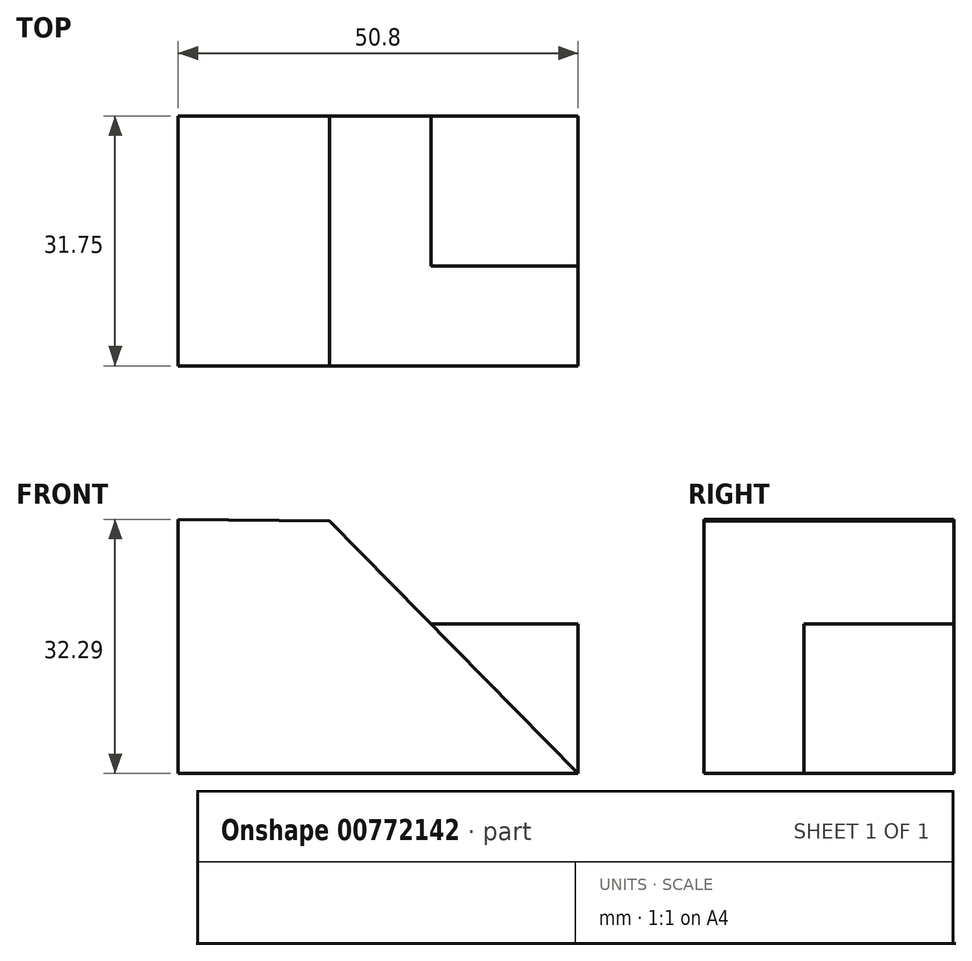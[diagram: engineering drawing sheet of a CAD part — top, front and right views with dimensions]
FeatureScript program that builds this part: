
annotation { "Feature Type Name" : "Feature", "Feature Type Description" : "" }
export const myFeature = defineFeature(function(context is Context, id is Id, definition is map)
    precondition{}
    {
        {
            var Q0;
            Q0=qCreatedBy(makeId("Front.planeOp"),FACE);
            var sketch = newSketch(context, id + "F0", { "sketchPlane" : qUnion([Q0])});
            skLineSegment(sketch, "E0", {"start": v(0, 32.3) * mm, "end": v(0, 0) * mm});
            skLineSegment(sketch, "E1", {"start": v(0, 0) * mm, "end": v(50.8, 0) * mm});
            skLineSegment(sketch, "E2", {"start": v(50.8, 0) * mm, "end": v(50.8, 31.75) * mm});
            skLineSegment(sketch, "E3", {"start": v(50.8, 31.75) * mm, "end": v(0, 32.3) * mm});
            skSolve(sketch);
        }
        {
            var Q0;
            Q0 = qSketchRegion(id + "F0", true);
            extrude(context, id + "F1", {"entities" : qUnion([Q0]), "depth" : 31.75 * mm, "offsetDistance" : 25.4 * mm});
        }
        {
            var Q0;
            Q0=makeQuery(id+"F1.opExtrude","CAP_FACE",FACE,{"disambiguationData":[OSD([sQuery(id+"F0.wireOp",EDGE,"E0"),sQuery(id+"F0.wireOp",EDGE,"E1"),sQuery(id+"F0.wireOp",EDGE,"E2"),sQuery(id+"F0.wireOp",EDGE,"E3")])],"isStart":false});
            var sketch = newSketch(context, id + "F2", { "sketchPlane" : qUnion([Q0])});
            skLineSegment(sketch, "E4", {"start": v(0, 32.3) * mm, "end": v(19.2, 32.09) * mm});
            skLineSegment(sketch, "E5", {"start": v(19.2, 32.09) * mm, "end": v(50.8, 0) * mm});
            skSolve(sketch);
        }
        {
            var Q0;
            {var subQ0=sQuery(id+"F2.wireOp",EDGE,"E5");Q0=makeQuery(id+"F2.imprint","IMPRINT",FACE,{"disambiguationData":[TD([[makeQuery(id+"F2.imprint","IMPRINT",EDGE,{"derivedFrom":subQ0}),1.0]])]});}
            extrude(context, id + "F3", {"entities" : qUnion([Q0]), "operationType" : NewBodyOperationType.REMOVE, "oppositeDirection" : true, "depth" : 12.7 * mm, "offsetDistance" : 25.4 * mm});
        }
        {
            var Q0;
            Q0=makeQuery(id+"F3.boolean.opBoolean","COPY",FACE,{"derivedFrom":makeQuery(id+"F3.opExtrude","CAP_FACE",FACE,{"disambiguationData":[OSD([sQuery(id+"F0.wireOp",EDGE,"E2"),sQuery(id+"F0.wireOp",EDGE,"E3"),sQuery(id+"F2.wireOp",EDGE,"E5")])],"isStart":false})});
            var sketch = newSketch(context, id + "F4", { "sketchPlane" : qUnion([Q0])});
            skLineSegment(sketch, "E6", {"start": v(50.8, 0) * mm, "end": v(50.8, 19) * mm});
            skLineSegment(sketch, "E7", {"start": v(50.8, 19) * mm, "end": v(32.1, 19) * mm});
            skSolve(sketch);
        }
        {
            var Q0;
            {var subQ0=sQuery(id+"F4.wireOp",EDGE,"E7");Q0=makeQuery(id+"F4.imprint","IMPRINT",FACE,{"disambiguationData":[TD([[makeQuery(id+"F4.imprint","IMPRINT",EDGE,{"derivedFrom":subQ0}),-1.0]])]});}
            extrude(context, id + "F5", {"entities" : qUnion([Q0]), "operationType" : NewBodyOperationType.REMOVE, "endBound" : BoundingType.THROUGH_ALL, "oppositeDirection" : true, "depth" : 25.4 * mm, "offsetDistance" : 25.4 * mm});
        }
    });
